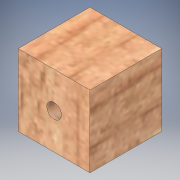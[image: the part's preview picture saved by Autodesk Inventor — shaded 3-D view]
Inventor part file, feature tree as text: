
AUTODESK INVENTOR PART (.ipt)
format: ipt  version: 2018 (Build 220112000, 112)  size: 136,192 bytes
history: native  units: in
note: dims shown in document units (in); Inventor stores cm internally (conversion verified against a paired STEP export)
features: extrude x1, sketch x1
ambient origin geometry x8: Origin, YZ Plane, XZ Plane, XY Plane, X Axis, Y Axis, Z Axis, Center Point
bodies: Solid1 (feature_tree)
feature tree (2):
  extrude  "Extrusion1"  Depth=1.0in
  sketch  "Sketch1"  dims[d0=1.0in d1=1.0in d2=0.2031in d3=1.0in d4=0.0in]
